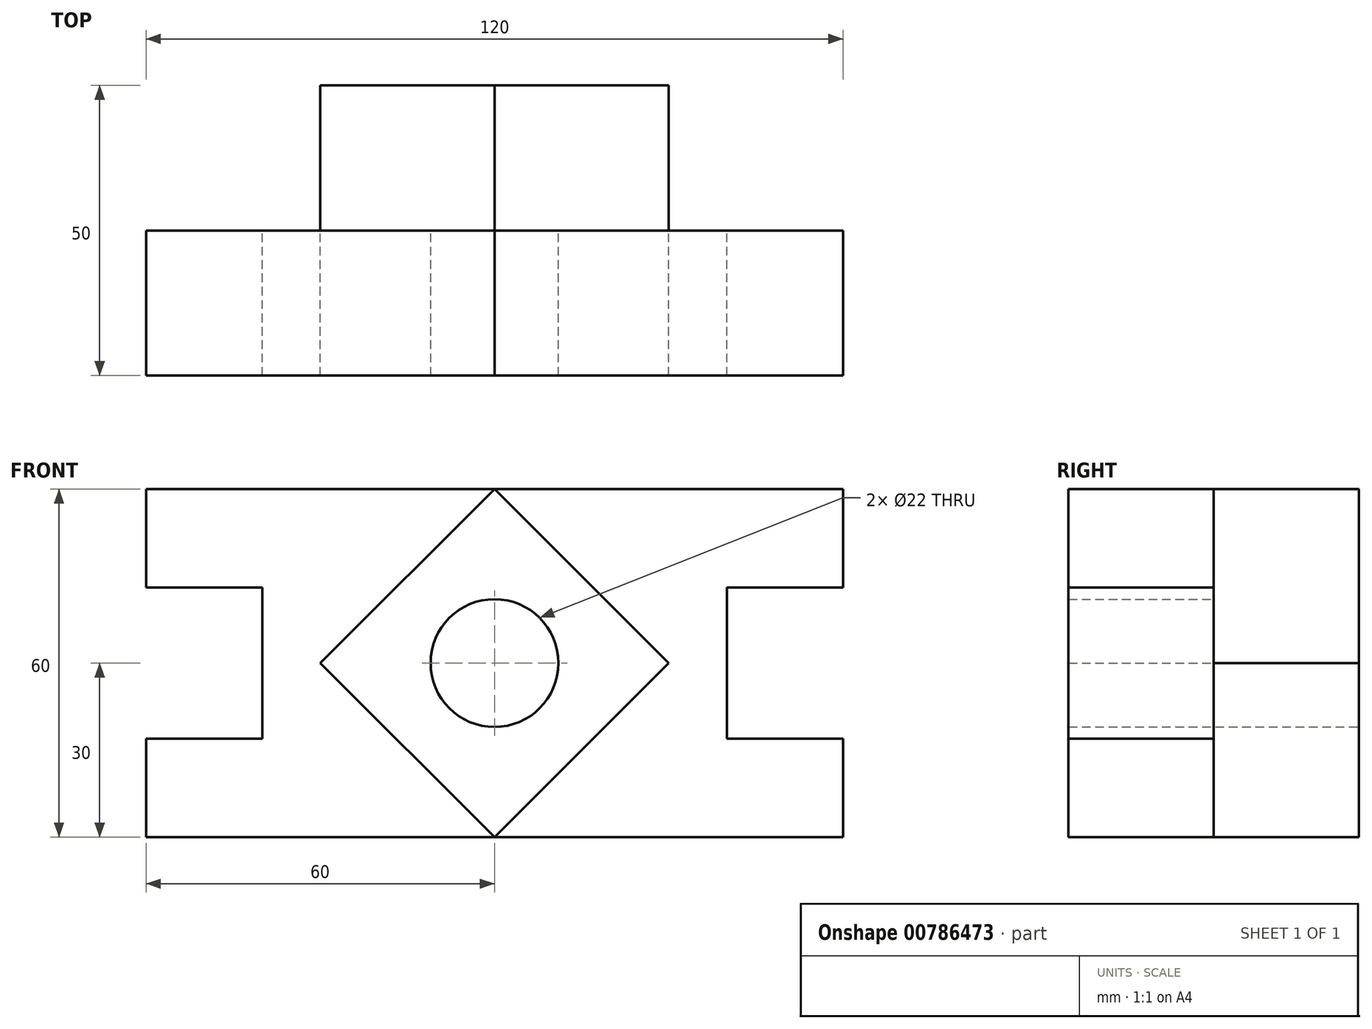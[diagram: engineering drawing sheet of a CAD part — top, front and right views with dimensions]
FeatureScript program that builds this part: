
annotation { "Feature Type Name" : "Feature", "Feature Type Description" : "" }
export const myFeature = defineFeature(function(context is Context, id is Id, definition is map)
    precondition{}
    {
        {
            var Q0;
            Q0=qCreatedBy(makeId("Front.planeOp"),FACE);
            var sketch = newSketch(context, id + "F0", { "sketchPlane" : qUnion([Q0])});
            skLineSegment(sketch, "E0.bottom", {"start": v(-60, -30) * mm, "end": v(-30, -30) * mm});
            skLineSegment(sketch, "E0.top", {"start": v(-60, 30) * mm, "end": v(60, 30) * mm});
            skLineSegment(sketch, "E0.left", {"start": v(-60, -30) * mm, "end": v(-60, -13) * mm});
            skLineSegment(sketch, "E0.right", {"start": v(60, -30) * mm, "end": v(60, -13) * mm});
            skPoint(sketch, "E0.middle", {"position": v(0, 0) * mm});
            skLineSegment(sketch, "E1", {"start": v(60, -13) * mm, "end": v(40, -13) * mm});
            skLineSegment(sketch, "E2", {"start": v(40, 13) * mm, "end": v(40, -13) * mm});
            skLineSegment(sketch, "E3", {"start": v(40, 13) * mm, "end": v(60, 13) * mm});
            skLineSegment(sketch, "E4", {"start": v(60, 13) * mm, "end": v(60, 30) * mm});
            skLineSegment(sketch, "E5", {"start": v(-60, -13) * mm, "end": v(-40, -13) * mm});
            skLineSegment(sketch, "E6", {"start": v(-40, -13) * mm, "end": v(-40, 13) * mm});
            skLineSegment(sketch, "E7", {"start": v(-40, 13) * mm, "end": v(-60, 13) * mm});
            skLineSegment(sketch, "E8.trimOffspring", {"start": v(-60, 13) * mm, "end": v(-60, 30) * mm});
            skLineSegment(sketch, "E9.bottom", {"start": v(-30, -30) * mm, "end": v(30, -30) * mm});
            skLineSegment(sketch, "E10", {"start": v(-30, 0) * mm, "end": v(0, -30) * mm});
            skLineSegment(sketch, "E11", {"start": v(0, -30) * mm, "end": v(30, 0) * mm});
            skLineSegment(sketch, "E12", {"start": v(30, 0) * mm, "end": v(0, 30) * mm});
            skLineSegment(sketch, "E13", {"start": v(0, 30) * mm, "end": v(-30, 0) * mm});
            skPoint(sketch, "E14.orphan", {"position": v(30, 30) * mm});
            skPoint(sketch, "E9.top.start.orphan", {"position": v(-30, 30) * mm});
            skLineSegment(sketch, "E15.trimOffspring", {"start": v(30, -30) * mm, "end": v(60, -30) * mm});
            skCircle(sketch, "E16", {"center": v(0, 0) * mm, "radius": 11 * mm});
            skSolve(sketch);
        }
        {
            var Q0;
            Q0 = qSketchRegion(id + "F0", true);
            extrude(context, id + "F1", {"entities" : qUnion([Q0]), "depth" : 25 * mm, "offsetDistance" : 25 * mm});
        }
        {
            var Q0;
            Q0=makeQuery(id+"F0.imprint","IMPRINT",FACE,{"disambiguationData":[TD([[makeQuery(id+"F0.imprint","IMPRINT",EDGE,{"derivedFrom":sQuery(id+"F0.wireOp",EDGE,"E10")}),1.0]])]});
            extrude(context, id + "F2", {"entities" : qUnion([Q0]), "endBound" : BoundingType.SYMMETRIC, "depth" : 50 * mm, "offsetDistance" : 25 * mm});
        }
    });
